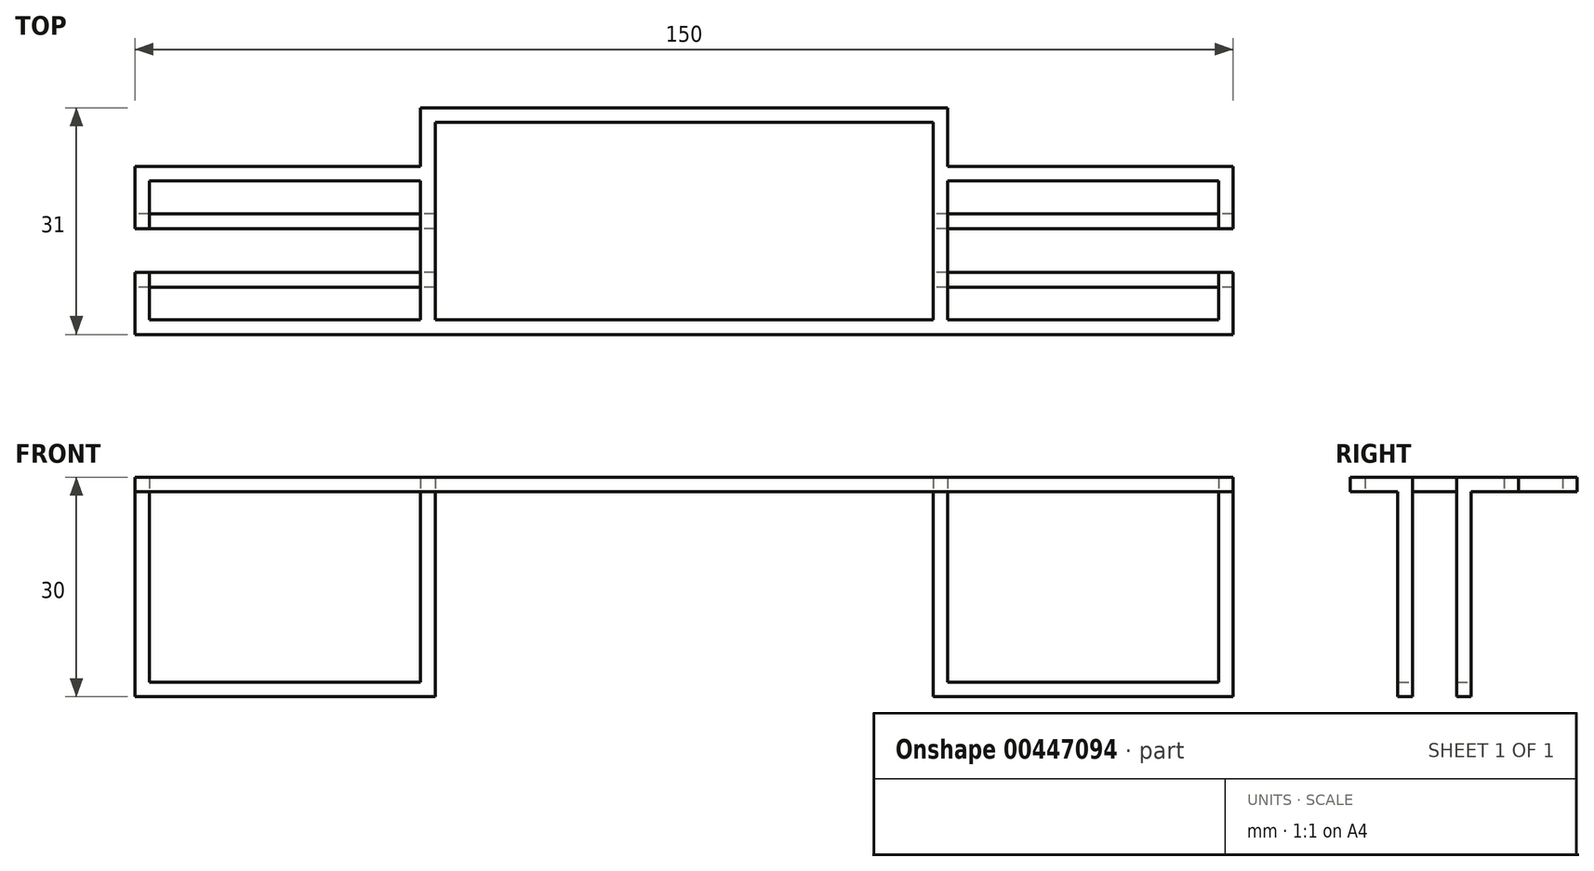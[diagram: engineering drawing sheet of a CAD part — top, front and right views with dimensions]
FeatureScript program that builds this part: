
annotation { "Feature Type Name" : "Feature", "Feature Type Description" : "" }
export const myFeature = defineFeature(function(context is Context, id is Id, definition is map)
    precondition{}
    {
        {
            var Q0;
            Q0=qCreatedBy(makeId("Top.planeOp"),FACE);
            var sketch = newSketch(context, id + "F0", { "sketchPlane" : qUnion([Q0])});
            skLineSegment(sketch, "E0", {"start": v(-73, 0) * mm, "end": v(73, 0) * mm});
            skLineSegment(sketch, "E1", {"start": v(73, 0) * mm, "end": v(73, 19) * mm});
            skLineSegment(sketch, "E2", {"start": v(73, 19) * mm, "end": v(34, 19) * mm});
            skLineSegment(sketch, "E3", {"start": v(34, 19) * mm, "end": v(34, 27) * mm});
            skLineSegment(sketch, "E4", {"start": v(34, 27) * mm, "end": v(-34, 27) * mm});
            skLineSegment(sketch, "E5", {"start": v(-34, 27) * mm, "end": v(-34, 19) * mm});
            skLineSegment(sketch, "E6", {"start": v(-34, 19) * mm, "end": v(-73, 19) * mm});
            skLineSegment(sketch, "E7", {"start": v(-73, 19) * mm, "end": v(-73, 0) * mm});
            skLineSegment(sketch, "E8.0", {"start": v(-36, 29) * mm, "end": v(-36, 21) * mm});
            skLineSegment(sketch, "E8.1", {"start": v(36, 29) * mm, "end": v(-36, 29) * mm});
            skLineSegment(sketch, "E8.2", {"start": v(-36, 21) * mm, "end": v(-75, 21) * mm});
            skLineSegment(sketch, "E8.3", {"start": v(36, 21) * mm, "end": v(36, 29) * mm});
            skLineSegment(sketch, "E8.4", {"start": v(-75, 21) * mm, "end": v(-75, -2) * mm});
            skLineSegment(sketch, "E8.5", {"start": v(-75, -2) * mm, "end": v(75, -2) * mm});
            skLineSegment(sketch, "E8.6", {"start": v(75, -2) * mm, "end": v(75, 21) * mm});
            skLineSegment(sketch, "E8.7", {"start": v(75, 21) * mm, "end": v(36, 21) * mm});
            skLineSegment(sketch, "E9", {"start": v(-36, 21) * mm, "end": v(-36, 0) * mm});
            skLineSegment(sketch, "E10", {"start": v(-34, 19) * mm, "end": v(-34, 0) * mm});
            skLineSegment(sketch, "E11", {"start": v(34, 19) * mm, "end": v(34, 0) * mm});
            skLineSegment(sketch, "E12", {"start": v(36, 21) * mm, "end": v(36, 0) * mm});
            skPoint(sketch, "E13", {"position": v(-75, 9.5) * mm});
            skLineSegment(sketch, "E14", {"start": v(-75, 9.5) * mm, "end": v(75, 9.5) * mm, "construction": true});
            skPoint(sketch, "E15", {"position": v(0, 9.5) * mm});
            skLineSegment(sketch, "E16.bottom", {"start": v(75, 4.5) * mm, "end": v(-75, 4.5) * mm});
            skLineSegment(sketch, "E16.top", {"start": v(75, 14.5) * mm, "end": v(-75, 14.5) * mm});
            skLineSegment(sketch, "E16.left", {"start": v(75, 4.5) * mm, "end": v(75, 14.5) * mm});
            skLineSegment(sketch, "E16.right", {"start": v(-75, 4.5) * mm, "end": v(-75, 14.5) * mm});
            skLineSegment(sketch, "E17.bottom", {"start": v(75, 6.5) * mm, "end": v(-75, 6.5) * mm});
            skLineSegment(sketch, "E17.top", {"start": v(75, 12.5) * mm, "end": v(-75, 12.5) * mm});
            skLineSegment(sketch, "E17.left", {"start": v(75, 6.5) * mm, "end": v(75, 12.5) * mm});
            skLineSegment(sketch, "E17.right", {"start": v(-75, 6.5) * mm, "end": v(-75, 12.5) * mm});
            skLineSegment(sketch, "E18.bottom", {"start": v(1, 6.5) * mm, "end": v(-1, 6.5) * mm});
            skLineSegment(sketch, "E18.top", {"start": v(1, 12.5) * mm, "end": v(-1, 12.5) * mm});
            skLineSegment(sketch, "E18.left", {"start": v(1, 6.5) * mm, "end": v(1, 12.5) * mm});
            skLineSegment(sketch, "E18.right", {"start": v(-1, 6.5) * mm, "end": v(-1, 12.5) * mm});
            skSolve(sketch);
        }
        {
            var Q0;
            {var subQ0=sQuery(id+"F0.wireOp",EDGE,"E16.top");var subQ1=sQuery(id+"F0.wireOp",EDGE,"E7");var subQ2=makeQuery(id+"F0.imprint","INTERSECT",VERTEX,{"derivedFrom":[subQ1,subQ0]});Q0=makeQuery(id+"F0.imprint","IMPRINT",FACE,{"disambiguationData":[TD([[makeQuery(id+"F0.imprint","IMPRINT",EDGE,{"disambiguationData":[TD([[subQ2,-1.0]])],"derivedFrom":subQ1}),-1.0]])]});}
            var Q1;
            {var subQ5=sQuery(id+"F0.wireOp",EDGE,"E17.right");Q1=makeQuery(id+"F0.imprint","IMPRINT",FACE,{"disambiguationData":[TD([[makeQuery(id+"F0.imprint","IMPRINT",EDGE,{"derivedFrom":subQ5}),-1.0]])]});}
            var Q2;
            {var subQ0=sQuery(id+"F0.wireOp",EDGE,"E17.bottom");var subQ1=sQuery(id+"F0.wireOp",EDGE,"E7");var subQ2=makeQuery(id+"F0.imprint","INTERSECT",VERTEX,{"derivedFrom":[subQ1,subQ0]});Q2=makeQuery(id+"F0.imprint","IMPRINT",FACE,{"disambiguationData":[TD([[makeQuery(id+"F0.imprint","IMPRINT",EDGE,{"disambiguationData":[TD([[subQ2,-1.0]])],"derivedFrom":subQ1}),-1.0]])]});}
            var Q3;
            {var subQ0=sQuery(id+"F0.wireOp",EDGE,"E17.bottom");var subQ1=sQuery(id+"F0.wireOp",EDGE,"E7");var subQ2=makeQuery(id+"F0.imprint","INTERSECT",VERTEX,{"derivedFrom":[subQ1,subQ0]});Q3=makeQuery(id+"F0.imprint","IMPRINT",FACE,{"disambiguationData":[TD([[makeQuery(id+"F0.imprint","IMPRINT",EDGE,{"disambiguationData":[TD([[subQ2,-1.0]])],"derivedFrom":subQ1}),1.0]])]});}
            var Q4;
            {var subQ0=sQuery(id+"F0.wireOp",EDGE,"E16.top");var subQ1=sQuery(id+"F0.wireOp",EDGE,"E7");var subQ2=makeQuery(id+"F0.imprint","INTERSECT",VERTEX,{"derivedFrom":[subQ1,subQ0]});Q4=makeQuery(id+"F0.imprint","IMPRINT",FACE,{"disambiguationData":[TD([[makeQuery(id+"F0.imprint","IMPRINT",EDGE,{"disambiguationData":[TD([[subQ2,-1.0]])],"derivedFrom":subQ1}),1.0]])]});}
            var Q5;
            {var subQ0=sQuery(id+"F0.wireOp",EDGE,"E16.top");var subQ1=sQuery(id+"F0.wireOp",EDGE,"E9");var subQ2=makeQuery(id+"F0.imprint","INTERSECT",VERTEX,{"derivedFrom":[subQ1,subQ0]});Q5=makeQuery(id+"F0.imprint","IMPRINT",FACE,{"disambiguationData":[TD([[makeQuery(id+"F0.imprint","IMPRINT",EDGE,{"disambiguationData":[TD([[subQ2,-1.0]])],"derivedFrom":subQ1}),1.0]])]});}
            var Q6;
            {var subQ0=sQuery(id+"F0.wireOp",EDGE,"E18.top");Q6=makeQuery(id+"F0.imprint","IMPRINT",FACE,{"disambiguationData":[TD([[makeQuery(id+"F0.imprint","IMPRINT",EDGE,{"derivedFrom":subQ0}),-1.0]])]});}
            var Q7;
            {var subQ0=sQuery(id+"F0.wireOp",EDGE,"E17.bottom");var subQ1=sQuery(id+"F0.wireOp",EDGE,"E9");var subQ2=makeQuery(id+"F0.imprint","INTERSECT",VERTEX,{"derivedFrom":[subQ1,subQ0]});Q7=makeQuery(id+"F0.imprint","IMPRINT",FACE,{"disambiguationData":[TD([[makeQuery(id+"F0.imprint","IMPRINT",EDGE,{"disambiguationData":[TD([[subQ2,-1.0]])],"derivedFrom":subQ1}),1.0]])]});}
            var Q8;
            {var subQ0=sQuery(id+"F0.wireOp",EDGE,"E18.bottom");Q8=makeQuery(id+"F0.imprint","IMPRINT",FACE,{"disambiguationData":[TD([[makeQuery(id+"F0.imprint","IMPRINT",EDGE,{"derivedFrom":subQ0}),1.0]])]});}
            var Q9;
            Q9=makeQuery(id+"F0.imprint","IMPRINT",FACE,{"disambiguationData":[TD([[makeQuery(id+"F0.imprint","IMPRINT",EDGE,{"derivedFrom":sQuery(id+"F0.wireOp",EDGE,"E18.bottom")}),-1.0]])]});
            var Q10;
            {var subQ0=sQuery(id+"F0.wireOp",EDGE,"E16.top");var subQ1=sQuery(id+"F0.wireOp",EDGE,"E11");var subQ2=makeQuery(id+"F0.imprint","INTERSECT",VERTEX,{"derivedFrom":[subQ1,subQ0]});Q10=makeQuery(id+"F0.imprint","IMPRINT",FACE,{"disambiguationData":[TD([[makeQuery(id+"F0.imprint","IMPRINT",EDGE,{"disambiguationData":[TD([[subQ2,-1.0]])],"derivedFrom":subQ1}),1.0]])]});}
            var Q11;
            {var subQ0=sQuery(id+"F0.wireOp",EDGE,"E17.bottom");var subQ1=sQuery(id+"F0.wireOp",EDGE,"E11");var subQ2=makeQuery(id+"F0.imprint","INTERSECT",VERTEX,{"derivedFrom":[subQ1,subQ0]});Q11=makeQuery(id+"F0.imprint","IMPRINT",FACE,{"disambiguationData":[TD([[makeQuery(id+"F0.imprint","IMPRINT",EDGE,{"disambiguationData":[TD([[subQ2,-1.0]])],"derivedFrom":subQ1}),1.0]])]});}
            var Q12;
            {var subQ0=sQuery(id+"F0.wireOp",EDGE,"E16.bottom");var subQ1=sQuery(id+"F0.wireOp",EDGE,"E1");var subQ2=makeQuery(id+"F0.imprint","INTERSECT",VERTEX,{"derivedFrom":[subQ1,subQ0]});Q12=makeQuery(id+"F0.imprint","IMPRINT",FACE,{"disambiguationData":[TD([[makeQuery(id+"F0.imprint","IMPRINT",EDGE,{"disambiguationData":[TD([[subQ2,-1.0]])],"derivedFrom":subQ1}),1.0]])]});}
            var Q13;
            {var subQ0=sQuery(id+"F0.wireOp",EDGE,"E17.top");var subQ1=sQuery(id+"F0.wireOp",EDGE,"E1");var subQ2=makeQuery(id+"F0.imprint","INTERSECT",VERTEX,{"derivedFrom":[subQ1,subQ0]});Q13=makeQuery(id+"F0.imprint","IMPRINT",FACE,{"disambiguationData":[TD([[makeQuery(id+"F0.imprint","IMPRINT",EDGE,{"disambiguationData":[TD([[subQ2,-1.0]])],"derivedFrom":subQ1}),1.0]])]});}
            var Q14;
            {var subQ0=sQuery(id+"F0.wireOp",EDGE,"E17.top");var subQ1=sQuery(id+"F0.wireOp",EDGE,"E1");var subQ2=makeQuery(id+"F0.imprint","INTERSECT",VERTEX,{"derivedFrom":[subQ1,subQ0]});Q14=makeQuery(id+"F0.imprint","IMPRINT",FACE,{"disambiguationData":[TD([[makeQuery(id+"F0.imprint","IMPRINT",EDGE,{"disambiguationData":[TD([[subQ2,-1.0]])],"derivedFrom":subQ1}),-1.0]])]});}
            var Q15;
            {var subQ5=sQuery(id+"F0.wireOp",EDGE,"E17.left");Q15=makeQuery(id+"F0.imprint","IMPRINT",FACE,{"disambiguationData":[TD([[makeQuery(id+"F0.imprint","IMPRINT",EDGE,{"derivedFrom":subQ5}),1.0]])]});}
            var Q16;
            {var subQ0=sQuery(id+"F0.wireOp",EDGE,"E16.bottom");var subQ1=sQuery(id+"F0.wireOp",EDGE,"E1");var subQ2=makeQuery(id+"F0.imprint","INTERSECT",VERTEX,{"derivedFrom":[subQ1,subQ0]});Q16=makeQuery(id+"F0.imprint","IMPRINT",FACE,{"disambiguationData":[TD([[makeQuery(id+"F0.imprint","IMPRINT",EDGE,{"disambiguationData":[TD([[subQ2,-1.0]])],"derivedFrom":subQ1}),-1.0]])]});}
            extrude(context, id + "F1", {"entities" : qUnion([Q0, Q1, Q2, Q3, Q4, Q5, Q6, Q7, Q8, Q9, Q10, Q11, Q12, Q13, Q14, Q15, Q16]), "depth" : 2 * mm, "offsetDistance" : 25 * mm});
        }
        {
            var Q0;
            {var subQ0=sQuery(id+"F0.wireOp",EDGE,"E17.bottom");var subQ1=sQuery(id+"F0.wireOp",EDGE,"E7");var subQ2=makeQuery(id+"F0.imprint","INTERSECT",VERTEX,{"derivedFrom":[subQ1,subQ0]});Q0=makeQuery(id+"F0.imprint","IMPRINT",FACE,{"disambiguationData":[TD([[makeQuery(id+"F0.imprint","IMPRINT",EDGE,{"disambiguationData":[TD([[subQ2,-1.0]])],"derivedFrom":subQ1}),-1.0]])]});}
            var Q1;
            {var subQ0=sQuery(id+"F0.wireOp",EDGE,"E16.top");var subQ1=sQuery(id+"F0.wireOp",EDGE,"E7");var subQ2=makeQuery(id+"F0.imprint","INTERSECT",VERTEX,{"derivedFrom":[subQ1,subQ0]});Q1=makeQuery(id+"F0.imprint","IMPRINT",FACE,{"disambiguationData":[TD([[makeQuery(id+"F0.imprint","IMPRINT",EDGE,{"disambiguationData":[TD([[subQ2,-1.0]])],"derivedFrom":subQ1}),-1.0]])]});}
            var Q2;
            {var subQ0=sQuery(id+"F0.wireOp",EDGE,"E17.bottom");var subQ1=sQuery(id+"F0.wireOp",EDGE,"E9");var subQ2=makeQuery(id+"F0.imprint","INTERSECT",VERTEX,{"derivedFrom":[subQ1,subQ0]});Q2=makeQuery(id+"F0.imprint","IMPRINT",FACE,{"disambiguationData":[TD([[makeQuery(id+"F0.imprint","IMPRINT",EDGE,{"disambiguationData":[TD([[subQ2,-1.0]])],"derivedFrom":subQ1}),1.0]])]});}
            var Q3;
            {var subQ0=sQuery(id+"F0.wireOp",EDGE,"E16.top");var subQ1=sQuery(id+"F0.wireOp",EDGE,"E9");var subQ2=makeQuery(id+"F0.imprint","INTERSECT",VERTEX,{"derivedFrom":[subQ1,subQ0]});Q3=makeQuery(id+"F0.imprint","IMPRINT",FACE,{"disambiguationData":[TD([[makeQuery(id+"F0.imprint","IMPRINT",EDGE,{"disambiguationData":[TD([[subQ2,-1.0]])],"derivedFrom":subQ1}),1.0]])]});}
            var Q4;
            {var subQ0=sQuery(id+"F0.wireOp",EDGE,"E17.bottom");var subQ1=sQuery(id+"F0.wireOp",EDGE,"E11");var subQ2=makeQuery(id+"F0.imprint","INTERSECT",VERTEX,{"derivedFrom":[subQ1,subQ0]});Q4=makeQuery(id+"F0.imprint","IMPRINT",FACE,{"disambiguationData":[TD([[makeQuery(id+"F0.imprint","IMPRINT",EDGE,{"disambiguationData":[TD([[subQ2,-1.0]])],"derivedFrom":subQ1}),1.0]])]});}
            var Q5;
            {var subQ0=sQuery(id+"F0.wireOp",EDGE,"E16.top");var subQ1=sQuery(id+"F0.wireOp",EDGE,"E11");var subQ2=makeQuery(id+"F0.imprint","INTERSECT",VERTEX,{"derivedFrom":[subQ1,subQ0]});Q5=makeQuery(id+"F0.imprint","IMPRINT",FACE,{"disambiguationData":[TD([[makeQuery(id+"F0.imprint","IMPRINT",EDGE,{"disambiguationData":[TD([[subQ2,-1.0]])],"derivedFrom":subQ1}),1.0]])]});}
            var Q6;
            {var subQ0=sQuery(id+"F0.wireOp",EDGE,"E16.bottom");var subQ1=sQuery(id+"F0.wireOp",EDGE,"E1");var subQ2=makeQuery(id+"F0.imprint","INTERSECT",VERTEX,{"derivedFrom":[subQ1,subQ0]});Q6=makeQuery(id+"F0.imprint","IMPRINT",FACE,{"disambiguationData":[TD([[makeQuery(id+"F0.imprint","IMPRINT",EDGE,{"disambiguationData":[TD([[subQ2,-1.0]])],"derivedFrom":subQ1}),-1.0]])]});}
            var Q7;
            {var subQ0=sQuery(id+"F0.wireOp",EDGE,"E17.top");var subQ1=sQuery(id+"F0.wireOp",EDGE,"E1");var subQ2=makeQuery(id+"F0.imprint","INTERSECT",VERTEX,{"derivedFrom":[subQ1,subQ0]});Q7=makeQuery(id+"F0.imprint","IMPRINT",FACE,{"disambiguationData":[TD([[makeQuery(id+"F0.imprint","IMPRINT",EDGE,{"disambiguationData":[TD([[subQ2,-1.0]])],"derivedFrom":subQ1}),-1.0]])]});}
            extrude(context, id + "F2", {"entities" : qUnion([Q0, Q1, Q2, Q3, Q4, Q5, Q6, Q7]), "operationType" : NewBodyOperationType.ADD, "depth" : 30 * mm, "offsetDistance" : 25 * mm});
        }
        {
            var Q0;
            {var subQ0=sQuery(id+"F0.wireOp",EDGE,"E8.2");Q0=makeQuery(id+"F0.imprint","IMPRINT",FACE,{"disambiguationData":[TD([[makeQuery(id+"F0.imprint","IMPRINT",EDGE,{"derivedFrom":subQ0}),1.0]])]});}
            var Q1;
            {var subQ1=sQuery(id+"F0.wireOp",EDGE,"E8.5");Q1=makeQuery(id+"F0.imprint","IMPRINT",FACE,{"disambiguationData":[TD([[makeQuery(id+"F0.imprint","IMPRINT",EDGE,{"derivedFrom":subQ1}),1.0]])]});}
            var Q2;
            {var subQ0=sQuery(id+"F0.wireOp",EDGE,"E9");var subQ1=sQuery(id+"F0.wireOp",EDGE,"E0");var subQ2=makeQuery(id+"F0.imprint","INTERSECT",VERTEX,{"derivedFrom":[subQ1,subQ0]});Q2=makeQuery(id+"F0.imprint","IMPRINT",FACE,{"disambiguationData":[TD([[makeQuery(id+"F0.imprint","IMPRINT",EDGE,{"disambiguationData":[TD([[subQ2,-1.0]])],"derivedFrom":subQ1}),1.0]])]});}
            var Q3;
            {var subQ0=sQuery(id+"F0.wireOp",EDGE,"E17.top");var subQ1=sQuery(id+"F0.wireOp",EDGE,"E9");var subQ2=makeQuery(id+"F0.imprint","INTERSECT",VERTEX,{"derivedFrom":[subQ1,subQ0]});Q3=makeQuery(id+"F0.imprint","IMPRINT",FACE,{"disambiguationData":[TD([[makeQuery(id+"F0.imprint","IMPRINT",EDGE,{"disambiguationData":[TD([[subQ2,-1.0]])],"derivedFrom":subQ1}),1.0]])]});}
            var Q4;
            {var subQ1=sQuery(id+"F0.wireOp",EDGE,"E6");var subQ3=sQuery(id+"F0.wireOp",EDGE,"E9");var subQ4=makeQuery(id+"F0.imprint","INTERSECT",VERTEX,{"derivedFrom":[subQ1,subQ3]});Q4=makeQuery(id+"F0.imprint","IMPRINT",FACE,{"disambiguationData":[TD([[makeQuery(id+"F0.imprint","IMPRINT",EDGE,{"disambiguationData":[TD([[subQ4,-1.0]])],"derivedFrom":subQ3}),1.0]])]});}
            var Q5;
            {var subQ2=sQuery(id+"F0.wireOp",EDGE,"E3");Q5=makeQuery(id+"F0.imprint","IMPRINT",FACE,{"disambiguationData":[TD([[makeQuery(id+"F0.imprint","IMPRINT",EDGE,{"derivedFrom":subQ2}),-1.0]])]});}
            var Q6;
            {var subQ1=sQuery(id+"F0.wireOp",EDGE,"E2");var subQ3=sQuery(id+"F0.wireOp",EDGE,"E12");var subQ4=makeQuery(id+"F0.imprint","INTERSECT",VERTEX,{"derivedFrom":[subQ1,subQ3]});Q6=makeQuery(id+"F0.imprint","IMPRINT",FACE,{"disambiguationData":[TD([[makeQuery(id+"F0.imprint","IMPRINT",EDGE,{"disambiguationData":[TD([[subQ4,-1.0]])],"derivedFrom":subQ3}),-1.0]])]});}
            var Q7;
            {var subQ0=sQuery(id+"F0.wireOp",EDGE,"E8.7");Q7=makeQuery(id+"F0.imprint","IMPRINT",FACE,{"disambiguationData":[TD([[makeQuery(id+"F0.imprint","IMPRINT",EDGE,{"derivedFrom":subQ0}),1.0]])]});}
            var Q8;
            {var subQ0=sQuery(id+"F0.wireOp",EDGE,"E17.top");var subQ1=sQuery(id+"F0.wireOp",EDGE,"E11");var subQ2=makeQuery(id+"F0.imprint","INTERSECT",VERTEX,{"derivedFrom":[subQ1,subQ0]});Q8=makeQuery(id+"F0.imprint","IMPRINT",FACE,{"disambiguationData":[TD([[makeQuery(id+"F0.imprint","IMPRINT",EDGE,{"disambiguationData":[TD([[subQ2,-1.0]])],"derivedFrom":subQ1}),1.0]])]});}
            var Q9;
            {var subQ0=sQuery(id+"F0.wireOp",EDGE,"E11");var subQ1=sQuery(id+"F0.wireOp",EDGE,"E0");var subQ2=makeQuery(id+"F0.imprint","INTERSECT",VERTEX,{"derivedFrom":[subQ1,subQ0]});Q9=makeQuery(id+"F0.imprint","IMPRINT",FACE,{"disambiguationData":[TD([[makeQuery(id+"F0.imprint","IMPRINT",EDGE,{"disambiguationData":[TD([[subQ2,-1.0]])],"derivedFrom":subQ1}),1.0]])]});}
            var Q10;
            {var subQ0=sQuery(id+"F0.wireOp",EDGE,"E17.bottom");var subQ1=sQuery(id+"F0.wireOp",EDGE,"E9");var subQ2=makeQuery(id+"F0.imprint","INTERSECT",VERTEX,{"derivedFrom":[subQ1,subQ0]});Q10=makeQuery(id+"F0.imprint","IMPRINT",FACE,{"disambiguationData":[TD([[makeQuery(id+"F0.imprint","IMPRINT",EDGE,{"disambiguationData":[TD([[subQ2,-1.0]])],"derivedFrom":subQ1}),1.0]])]});}
            var Q11;
            {var subQ0=sQuery(id+"F0.wireOp",EDGE,"E17.bottom");var subQ1=sQuery(id+"F0.wireOp",EDGE,"E7");var subQ2=makeQuery(id+"F0.imprint","INTERSECT",VERTEX,{"derivedFrom":[subQ1,subQ0]});Q11=makeQuery(id+"F0.imprint","IMPRINT",FACE,{"disambiguationData":[TD([[makeQuery(id+"F0.imprint","IMPRINT",EDGE,{"disambiguationData":[TD([[subQ2,-1.0]])],"derivedFrom":subQ1}),-1.0]])]});}
            var Q12;
            {var subQ5=sQuery(id+"F0.wireOp",EDGE,"E17.right");Q12=makeQuery(id+"F0.imprint","IMPRINT",FACE,{"disambiguationData":[TD([[makeQuery(id+"F0.imprint","IMPRINT",EDGE,{"derivedFrom":subQ5}),-1.0]])]});}
            var Q13;
            {var subQ0=sQuery(id+"F0.wireOp",EDGE,"E16.top");var subQ1=sQuery(id+"F0.wireOp",EDGE,"E7");var subQ2=makeQuery(id+"F0.imprint","INTERSECT",VERTEX,{"derivedFrom":[subQ1,subQ0]});Q13=makeQuery(id+"F0.imprint","IMPRINT",FACE,{"disambiguationData":[TD([[makeQuery(id+"F0.imprint","IMPRINT",EDGE,{"disambiguationData":[TD([[subQ2,-1.0]])],"derivedFrom":subQ1}),-1.0]])]});}
            var Q14;
            {var subQ0=sQuery(id+"F0.wireOp",EDGE,"E16.top");var subQ1=sQuery(id+"F0.wireOp",EDGE,"E9");var subQ2=makeQuery(id+"F0.imprint","INTERSECT",VERTEX,{"derivedFrom":[subQ1,subQ0]});Q14=makeQuery(id+"F0.imprint","IMPRINT",FACE,{"disambiguationData":[TD([[makeQuery(id+"F0.imprint","IMPRINT",EDGE,{"disambiguationData":[TD([[subQ2,-1.0]])],"derivedFrom":subQ1}),1.0]])]});}
            var Q15;
            {var subQ0=sQuery(id+"F0.wireOp",EDGE,"E16.top");var subQ1=sQuery(id+"F0.wireOp",EDGE,"E11");var subQ2=makeQuery(id+"F0.imprint","INTERSECT",VERTEX,{"derivedFrom":[subQ1,subQ0]});Q15=makeQuery(id+"F0.imprint","IMPRINT",FACE,{"disambiguationData":[TD([[makeQuery(id+"F0.imprint","IMPRINT",EDGE,{"disambiguationData":[TD([[subQ2,-1.0]])],"derivedFrom":subQ1}),1.0]])]});}
            var Q16;
            {var subQ0=sQuery(id+"F0.wireOp",EDGE,"E17.bottom");var subQ1=sQuery(id+"F0.wireOp",EDGE,"E11");var subQ2=makeQuery(id+"F0.imprint","INTERSECT",VERTEX,{"derivedFrom":[subQ1,subQ0]});Q16=makeQuery(id+"F0.imprint","IMPRINT",FACE,{"disambiguationData":[TD([[makeQuery(id+"F0.imprint","IMPRINT",EDGE,{"disambiguationData":[TD([[subQ2,-1.0]])],"derivedFrom":subQ1}),1.0]])]});}
            var Q17;
            {var subQ0=sQuery(id+"F0.wireOp",EDGE,"E16.bottom");var subQ1=sQuery(id+"F0.wireOp",EDGE,"E1");var subQ2=makeQuery(id+"F0.imprint","INTERSECT",VERTEX,{"derivedFrom":[subQ1,subQ0]});Q17=makeQuery(id+"F0.imprint","IMPRINT",FACE,{"disambiguationData":[TD([[makeQuery(id+"F0.imprint","IMPRINT",EDGE,{"disambiguationData":[TD([[subQ2,-1.0]])],"derivedFrom":subQ1}),-1.0]])]});}
            var Q18;
            {var subQ5=sQuery(id+"F0.wireOp",EDGE,"E17.left");Q18=makeQuery(id+"F0.imprint","IMPRINT",FACE,{"disambiguationData":[TD([[makeQuery(id+"F0.imprint","IMPRINT",EDGE,{"derivedFrom":subQ5}),1.0]])]});}
            var Q19;
            {var subQ0=sQuery(id+"F0.wireOp",EDGE,"E17.top");var subQ1=sQuery(id+"F0.wireOp",EDGE,"E1");var subQ2=makeQuery(id+"F0.imprint","INTERSECT",VERTEX,{"derivedFrom":[subQ1,subQ0]});Q19=makeQuery(id+"F0.imprint","IMPRINT",FACE,{"disambiguationData":[TD([[makeQuery(id+"F0.imprint","IMPRINT",EDGE,{"disambiguationData":[TD([[subQ2,-1.0]])],"derivedFrom":subQ1}),-1.0]])]});}
            extrude(context, id + "F3", {"entities" : qUnion([Q0, Q1, Q2, Q3, Q4, Q5, Q6, Q7, Q8, Q9, Q10, Q11, Q12, Q13, Q14, Q15, Q16, Q17, Q18, Q19]), "operationType" : NewBodyOperationType.ADD, "depth" : 30 * mm, "offsetDistance" : 25 * mm, "hasSecondDirection" : true, "secondDirectionOppositeDirection" : false, "secondDirectionDepth" : 28 * mm});
        }
    });
